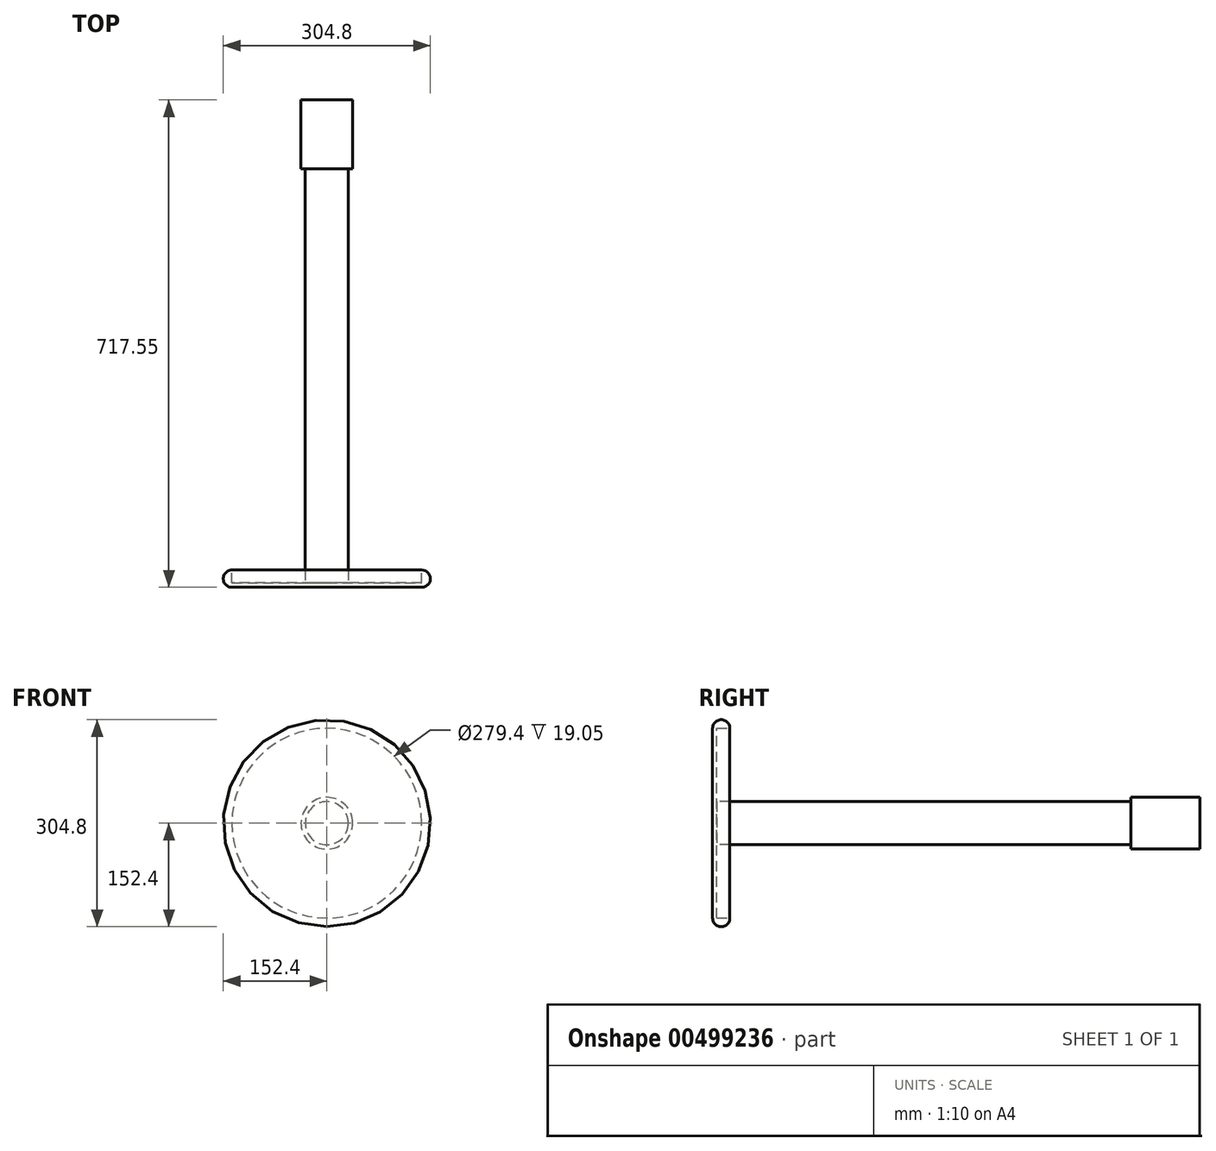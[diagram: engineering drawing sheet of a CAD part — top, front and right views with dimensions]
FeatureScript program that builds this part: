
annotation { "Feature Type Name" : "Feature", "Feature Type Description" : "" }
export const myFeature = defineFeature(function(context is Context, id is Id, definition is map)
    precondition{}
    {
        {
            var Q0;
            Q0=qCreatedBy(makeId("Front.planeOp"),FACE);
            var sketch = newSketch(context, id + "F0", { "sketchPlane" : qUnion([Q0])});
            skCircle(sketch, "E0", {"center": v(0, 0) * mm, "radius": 152.4 * mm});
            skSolve(sketch);
        }
        {
            var Q0;
            Q0 = qSketchRegion(id + "F0", true);
            extrude(context, id + "F1", {"entities" : qUnion([Q0]), "depth" : 25.4 * mm, "offsetDistance" : 25.4 * mm});
        }
        {
            var Q0;
            Q0=makeQuery(id+"F1.opExtrude","CAP_EDGE",EDGE,{"disambiguationData":[OSD([sQuery(id+"F0.wireOp",EDGE,"E0")])],"isStart":false});
            var Q1;
            Q1=makeQuery(id+"F1.opExtrude","CAP_EDGE",EDGE,{"disambiguationData":[OSD([sQuery(id+"F0.wireOp",EDGE,"E0")])],"isStart":true});
            fillet(context, id + "F2", {"entities" : qUnion([Q0, Q1]), "radius" : 12.7 * mm, "tangentPropagation" : true, "allowEdgeOverflow" : false});
        }
        {
            var Q0;
            Q0=makeQuery(id+"F1.opExtrude","CAP_FACE",FACE,{"disambiguationData":[OSD([sQuery(id+"F0.wireOp",EDGE,"E0")])],"isStart":true});
            var sketch = newSketch(context, id + "F3", { "sketchPlane" : qUnion([Q0])});
            skCircle(sketch, "E1", {"center": v(0, 0) * mm, "radius": 139.7 * mm});
            skSolve(sketch);
        }
        {
            var Q0;
            Q0 = qSketchRegion(id + "F3", true);
            extrude(context, id + "F4", {"entities" : qUnion([Q0]), "operationType" : NewBodyOperationType.REMOVE, "oppositeDirection" : true, "depth" : 19.05 * mm, "offsetDistance" : 25.4 * mm});
        }
        {
            var Q0;
            Q0=makeQuery(id+"F4.boolean.opBoolean","COPY",FACE,{"derivedFrom":makeQuery(id+"F4.opExtrude","CAP_FACE",FACE,{"disambiguationData":[OSD([sQuery(id+"F3.wireOp",EDGE,"E1")])],"isStart":false})});
            var sketch = newSketch(context, id + "F5", { "sketchPlane" : qUnion([Q0])});
            skCircle(sketch, "E2", {"center": v(0, 0) * mm, "radius": 31.75 * mm});
            skSolve(sketch);
        }
        {
            var Q0;
            Q0 = qSketchRegion(id + "F5", true);
            extrude(context, id + "F6", {"entities" : qUnion([Q0]), "operationType" : NewBodyOperationType.ADD, "depth" : 609.6 * mm, "offsetDistance" : 25.4 * mm});
        }
        {
            var Q0;
            Q0=makeQuery(id+"F6.opExtrude","CAP_FACE",FACE,{"disambiguationData":[OSD([sQuery(id+"F5.wireOp",EDGE,"E2")])],"isStart":false});
            var sketch = newSketch(context, id + "F7", { "sketchPlane" : qUnion([Q0])});
            skCircle(sketch, "E3", {"center": v(0, 0) * mm, "radius": 38.1 * mm});
            skSolve(sketch);
        }
        {
            var Q0;
            Q0 = qSketchRegion(id + "F7", true);
            extrude(context, id + "F8", {"entities" : qUnion([Q0]), "depth" : 101.6 * mm, "offsetDistance" : 25.4 * mm});
        }
    });
